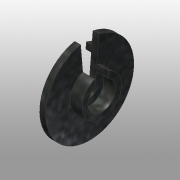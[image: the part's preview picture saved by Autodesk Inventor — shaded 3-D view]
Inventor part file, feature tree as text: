
AUTODESK INVENTOR PART (.ipt)
format: ipt  version: 2015 (Build 190159000, 159)  size: 129,024 bytes
history: native  units: mm
features: other x3, sketch x2
ambient origin geometry x8: Origin, YZ Plane, XZ Plane, XY Plane, X Axis, Y Axis, Z Axis, Center Point
bodies: Solid1 (feature_tree)
feature tree (5):
  other  "500-105.ipt"
  other  "Solid2::500-105.ipt"
  other  "TaggingFeature1"
  sketch  "Sketch1"  dims[d0=10.0mm]
  sketch  "Sketch2"
